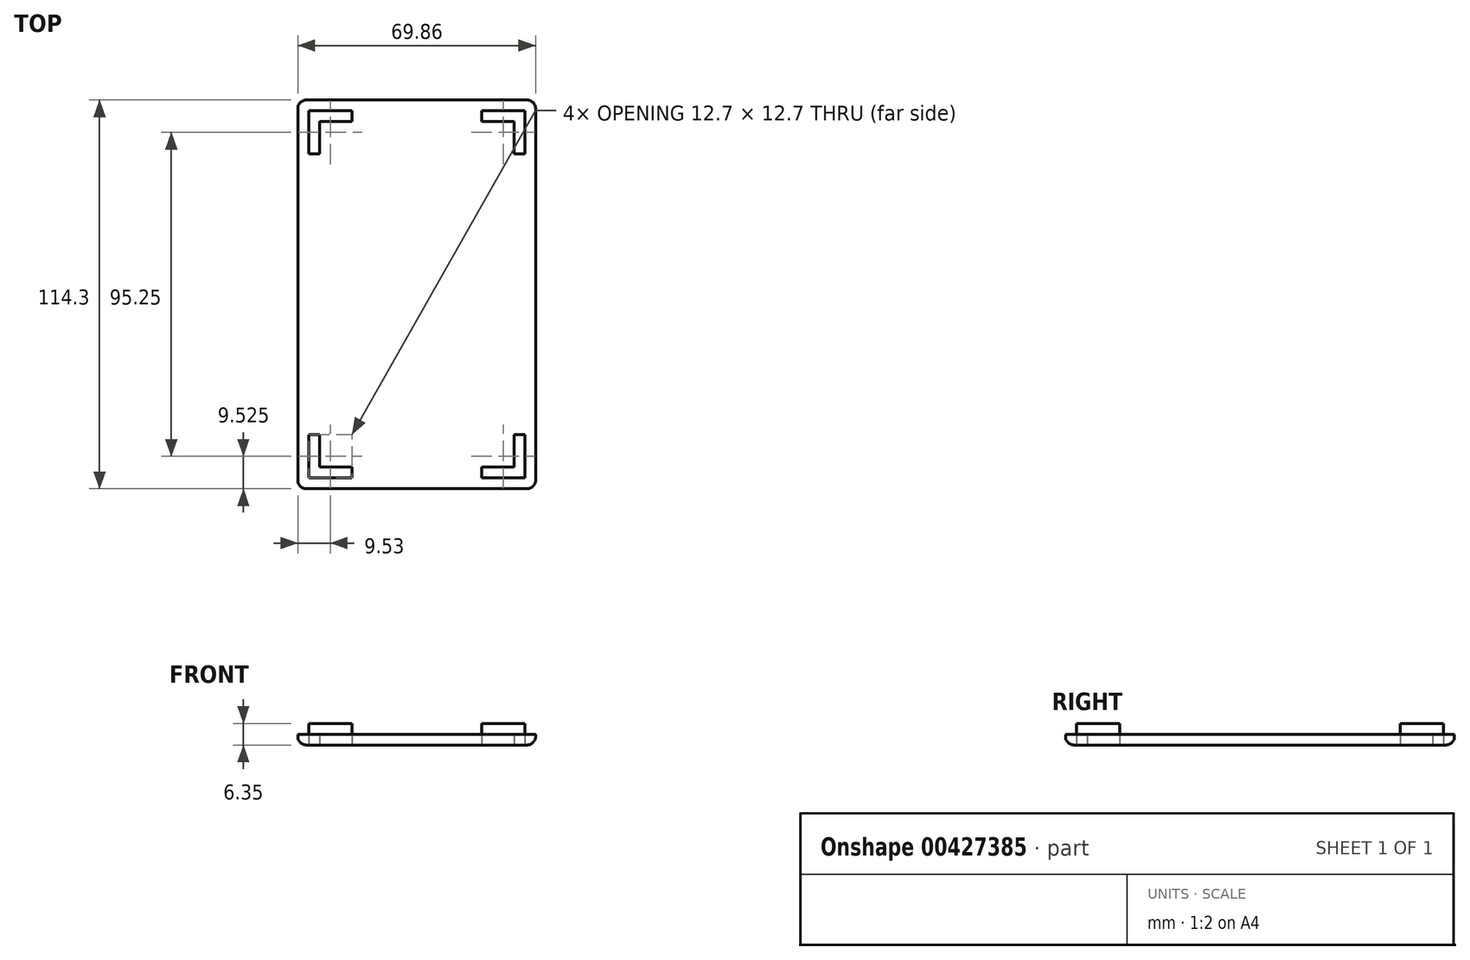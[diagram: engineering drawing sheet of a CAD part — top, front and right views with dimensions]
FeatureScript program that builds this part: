
annotation { "Feature Type Name" : "Feature", "Feature Type Description" : "" }
export const myFeature = defineFeature(function(context is Context, id is Id, definition is map)
    precondition{}
    {
        {
            var Q0;
            Q0=qCreatedBy(makeId("Top.planeOp"),FACE);
            var sketch = newSketch(context, id + "F0", { "sketchPlane" : qUnion([Q0])});
            skLineSegment(sketch, "E0.bottom", {"start": v(-34.92, 57.15) * mm, "end": v(34.93, 57.15) * mm});
            skLineSegment(sketch, "E0.top", {"start": v(-34.93, -57.15) * mm, "end": v(34.92, -57.15) * mm});
            skLineSegment(sketch, "E0.left", {"start": v(-34.92, 57.15) * mm, "end": v(-34.93, -57.15) * mm});
            skLineSegment(sketch, "E0.right", {"start": v(34.93, 57.15) * mm, "end": v(34.92, -57.15) * mm});
            skPoint(sketch, "E0.middle", {"position": v(0, 0) * mm});
            skLineSegment(sketch, "E1.bottom", {"start": v(-31.75, 53.98) * mm, "end": v(-19.05, 53.98) * mm});
            skLineSegment(sketch, "E1.top", {"start": v(-31.75, -53.98) * mm, "end": v(-19.05, -53.98) * mm});
            skLineSegment(sketch, "E1.right", {"start": v(31.75, 53.98) * mm, "end": v(31.75, 41.28) * mm});
            skLineSegment(sketch, "E2.bottom", {"start": v(-28.58, 50.8) * mm, "end": v(-19.05, 50.8) * mm});
            skLineSegment(sketch, "E2.top", {"start": v(-28.58, -50.8) * mm, "end": v(-19.05, -50.8) * mm});
            skLineSegment(sketch, "E2.left", {"start": v(-28.57, 50.8) * mm, "end": v(-28.57, 41.28) * mm});
            skLineSegment(sketch, "E2.right", {"start": v(28.58, 50.8) * mm, "end": v(28.58, 41.28) * mm});
            skLineSegment(sketch, "E3", {"start": v(-28.58, 41.28) * mm, "end": v(-31.75, 41.28) * mm});
            skLineSegment(sketch, "E4", {"start": v(-19.05, 53.98) * mm, "end": v(-19.05, 50.8) * mm});
            skLineSegment(sketch, "E5", {"start": v(19.05, 53.98) * mm, "end": v(19.05, 50.8) * mm});
            skLineSegment(sketch, "E6", {"start": v(28.58, 41.28) * mm, "end": v(31.75, 41.28) * mm});
            skLineSegment(sketch, "E7", {"start": v(28.58, -41.28) * mm, "end": v(31.75, -41.28) * mm});
            skLineSegment(sketch, "E8", {"start": v(19.05, -50.8) * mm, "end": v(19.05, -53.98) * mm});
            skLineSegment(sketch, "E9", {"start": v(-19.05, -50.8) * mm, "end": v(-19.05, -53.98) * mm});
            skLineSegment(sketch, "E10", {"start": v(-31.75, -41.28) * mm, "end": v(-28.58, -41.28) * mm});
            skLineSegment(sketch, "E11.trimOffspring", {"start": v(19.05, 53.98) * mm, "end": v(31.75, 53.98) * mm});
            skLineSegment(sketch, "E12.trimOffspring", {"start": v(19.05, 50.8) * mm, "end": v(28.58, 50.8) * mm});
            skLineSegment(sketch, "E13.trimOffspring", {"start": v(-31.75, -41.28) * mm, "end": v(-31.75, -53.98) * mm});
            skLineSegment(sketch, "E14.trimOffspring", {"start": v(-28.58, -41.28) * mm, "end": v(-28.58, -50.8) * mm});
            skLineSegment(sketch, "E15.trimOffspring", {"start": v(19.05, -50.8) * mm, "end": v(28.58, -50.8) * mm});
            skLineSegment(sketch, "E16.trimOffspring", {"start": v(19.05, -53.98) * mm, "end": v(31.75, -53.98) * mm});
            skLineSegment(sketch, "E17.trimOffspring", {"start": v(28.57, -41.28) * mm, "end": v(28.57, -50.8) * mm});
            skLineSegment(sketch, "E18.trimOffspring", {"start": v(31.75, -41.28) * mm, "end": v(31.75, -53.98) * mm});
            skLineSegment(sketch, "E19", {"start": v(-31.75, 41.28) * mm, "end": v(-31.75, 53.98) * mm});
            skSolve(sketch);
        }
        {
            var Q0;
            Q0=makeQuery(id+"F0.imprint","IMPRINT",FACE,{"disambiguationData":[TD([[makeQuery(id+"F0.imprint","IMPRINT",EDGE,{"derivedFrom":sQuery(id+"F0.wireOp",EDGE,"E1.bottom")}),-1.0]])]});
            var Q1;
            Q1=makeQuery(id+"F0.imprint","IMPRINT",FACE,{"disambiguationData":[TD([[makeQuery(id+"F0.imprint","IMPRINT",EDGE,{"derivedFrom":sQuery(id+"F0.wireOp",EDGE,"E1.right")}),-1.0]])]});
            var Q2;
            Q2=makeQuery(id+"F0.imprint","IMPRINT",FACE,{"disambiguationData":[TD([[makeQuery(id+"F0.imprint","IMPRINT",EDGE,{"derivedFrom":sQuery(id+"F0.wireOp",EDGE,"E7")}),-1.0]])]});
            var Q3;
            Q3=makeQuery(id+"F0.imprint","IMPRINT",FACE,{"disambiguationData":[TD([[makeQuery(id+"F0.imprint","IMPRINT",EDGE,{"derivedFrom":sQuery(id+"F0.wireOp",EDGE,"E1.top")}),1.0]])]});
            extrude(context, id + "F1", {"entities" : qUnion([Q0, Q1, Q2, Q3]), "depth" : 6.35 * mm});
        }
        {
            var Q0;
            Q0=makeQuery(id+"F0.imprint","IMPRINT",FACE,{"disambiguationData":[TD([[makeQuery(id+"F0.imprint","IMPRINT",EDGE,{"derivedFrom":sQuery(id+"F0.wireOp",EDGE,"E0.bottom")}),-1.0]])]});
            extrude(context, id + "F2", {"entities" : qUnion([Q0]), "depth" : 3.17 * mm});
        }
        {
            var Q0;
            Q0=makeQuery(id+"F2.opExtrude","SWEPT_EDGE",EDGE,{"disambiguationData":[OSD([sQuery(id+"F0.wireOp",EDGE,"E0.top"),sQuery(id+"F0.wireOp",EDGE,"E0.left")])]});
            var Q1;
            Q1=makeQuery(id+"F2.opExtrude","SWEPT_EDGE",EDGE,{"disambiguationData":[OSD([sQuery(id+"F0.wireOp",EDGE,"E0.bottom"),sQuery(id+"F0.wireOp",EDGE,"E0.left")])]});
            var Q2;
            Q2=makeQuery(id+"F2.opExtrude","SWEPT_EDGE",EDGE,{"disambiguationData":[OSD([sQuery(id+"F0.wireOp",EDGE,"E0.bottom"),sQuery(id+"F0.wireOp",EDGE,"E0.right")])]});
            var Q3;
            Q3=makeQuery(id+"F2.opExtrude","SWEPT_EDGE",EDGE,{"disambiguationData":[OSD([sQuery(id+"F0.wireOp",EDGE,"E0.top"),sQuery(id+"F0.wireOp",EDGE,"E0.right")])]});
            fillet(context, id + "F3", {"entities" : qUnion([Q0, Q1, Q2, Q3]), "radius" : 2.5 * mm, "tangentPropagation" : true, "allowEdgeOverflow" : false});
        }
        {
            var Q0;
            Q0=makeQuery(id+"F2.opExtrude","CAP_EDGE",EDGE,{"disambiguationData":[OSD([sQuery(id+"F0.wireOp",EDGE,"E0.top")])],"isStart":true});
            var Q1;
            {var subQ0=sQuery(id+"F0.wireOp",EDGE,"E0.right");var subQ1=sQuery(id+"F0.wireOp",EDGE,"E0.top");Q1=makeQuery(id+"F3.opFillet","BLEND_EDGE",EDGE,{"blendedFrom":[makeQuery(id+"F2.opExtrude","SWEPT_EDGE",EDGE,{"disambiguationData":[OSD([subQ1,subQ0])]}),makeQuery(id+"F2.opExtrude","CAP_FACE",FACE,{"disambiguationData":[OSD([sQuery(id+"F0.wireOp",EDGE,"E0.bottom"),subQ1,sQuery(id+"F0.wireOp",EDGE,"E0.left"),subQ0,sQuery(id+"F0.wireOp",EDGE,"E1.bottom"),sQuery(id+"F0.wireOp",EDGE,"E1.top"),sQuery(id+"F0.wireOp",EDGE,"E1.right"),sQuery(id+"F0.wireOp",EDGE,"E2.bottom"),sQuery(id+"F0.wireOp",EDGE,"E2.top"),sQuery(id+"F0.wireOp",EDGE,"E2.left"),sQuery(id+"F0.wireOp",EDGE,"E2.right"),sQuery(id+"F0.wireOp",EDGE,"E3"),sQuery(id+"F0.wireOp",EDGE,"E4"),sQuery(id+"F0.wireOp",EDGE,"E5"),sQuery(id+"F0.wireOp",EDGE,"E6"),sQuery(id+"F0.wireOp",EDGE,"E7"),sQuery(id+"F0.wireOp",EDGE,"E8"),sQuery(id+"F0.wireOp",EDGE,"E9"),sQuery(id+"F0.wireOp",EDGE,"E10"),sQuery(id+"F0.wireOp",EDGE,"E11.trimOffspring"),sQuery(id+"F0.wireOp",EDGE,"E12.trimOffspring"),sQuery(id+"F0.wireOp",EDGE,"E13.trimOffspring"),sQuery(id+"F0.wireOp",EDGE,"E14.trimOffspring"),sQuery(id+"F0.wireOp",EDGE,"E15.trimOffspring"),sQuery(id+"F0.wireOp",EDGE,"E16.trimOffspring"),sQuery(id+"F0.wireOp",EDGE,"E17.trimOffspring"),sQuery(id+"F0.wireOp",EDGE,"E18.trimOffspring"),sQuery(id+"F0.wireOp",EDGE,"E19")])],"isStart":true})],"blendedInto":[makeQuery(id+"F2.opExtrude","CAP_FACE",FACE,{"disambiguationData":[OSD([sQuery(id+"F0.wireOp",EDGE,"E0.bottom"),subQ1,sQuery(id+"F0.wireOp",EDGE,"E0.left"),subQ0,sQuery(id+"F0.wireOp",EDGE,"E1.bottom"),sQuery(id+"F0.wireOp",EDGE,"E1.top"),sQuery(id+"F0.wireOp",EDGE,"E1.right"),sQuery(id+"F0.wireOp",EDGE,"E2.bottom"),sQuery(id+"F0.wireOp",EDGE,"E2.top"),sQuery(id+"F0.wireOp",EDGE,"E2.left"),sQuery(id+"F0.wireOp",EDGE,"E2.right"),sQuery(id+"F0.wireOp",EDGE,"E3"),sQuery(id+"F0.wireOp",EDGE,"E4"),sQuery(id+"F0.wireOp",EDGE,"E5"),sQuery(id+"F0.wireOp",EDGE,"E6"),sQuery(id+"F0.wireOp",EDGE,"E7"),sQuery(id+"F0.wireOp",EDGE,"E8"),sQuery(id+"F0.wireOp",EDGE,"E9"),sQuery(id+"F0.wireOp",EDGE,"E10"),sQuery(id+"F0.wireOp",EDGE,"E11.trimOffspring"),sQuery(id+"F0.wireOp",EDGE,"E12.trimOffspring"),sQuery(id+"F0.wireOp",EDGE,"E13.trimOffspring"),sQuery(id+"F0.wireOp",EDGE,"E14.trimOffspring"),sQuery(id+"F0.wireOp",EDGE,"E15.trimOffspring"),sQuery(id+"F0.wireOp",EDGE,"E16.trimOffspring"),sQuery(id+"F0.wireOp",EDGE,"E17.trimOffspring"),sQuery(id+"F0.wireOp",EDGE,"E18.trimOffspring"),sQuery(id+"F0.wireOp",EDGE,"E19")])],"isStart":true})]});}
            var Q2;
            Q2=makeQuery(id+"F2.opExtrude","CAP_EDGE",EDGE,{"disambiguationData":[OSD([sQuery(id+"F0.wireOp",EDGE,"E0.right")])],"isStart":true});
            var Q3;
            {var subQ0=sQuery(id+"F0.wireOp",EDGE,"E0.right");var subQ1=sQuery(id+"F0.wireOp",EDGE,"E0.bottom");Q3=makeQuery(id+"F3.opFillet","BLEND_EDGE",EDGE,{"blendedFrom":[makeQuery(id+"F2.opExtrude","SWEPT_EDGE",EDGE,{"disambiguationData":[OSD([subQ1,subQ0])]}),makeQuery(id+"F2.opExtrude","CAP_FACE",FACE,{"disambiguationData":[OSD([subQ1,sQuery(id+"F0.wireOp",EDGE,"E0.top"),sQuery(id+"F0.wireOp",EDGE,"E0.left"),subQ0,sQuery(id+"F0.wireOp",EDGE,"E1.bottom"),sQuery(id+"F0.wireOp",EDGE,"E1.top"),sQuery(id+"F0.wireOp",EDGE,"E1.right"),sQuery(id+"F0.wireOp",EDGE,"E2.bottom"),sQuery(id+"F0.wireOp",EDGE,"E2.top"),sQuery(id+"F0.wireOp",EDGE,"E2.left"),sQuery(id+"F0.wireOp",EDGE,"E2.right"),sQuery(id+"F0.wireOp",EDGE,"E3"),sQuery(id+"F0.wireOp",EDGE,"E4"),sQuery(id+"F0.wireOp",EDGE,"E5"),sQuery(id+"F0.wireOp",EDGE,"E6"),sQuery(id+"F0.wireOp",EDGE,"E7"),sQuery(id+"F0.wireOp",EDGE,"E8"),sQuery(id+"F0.wireOp",EDGE,"E9"),sQuery(id+"F0.wireOp",EDGE,"E10"),sQuery(id+"F0.wireOp",EDGE,"E11.trimOffspring"),sQuery(id+"F0.wireOp",EDGE,"E12.trimOffspring"),sQuery(id+"F0.wireOp",EDGE,"E13.trimOffspring"),sQuery(id+"F0.wireOp",EDGE,"E14.trimOffspring"),sQuery(id+"F0.wireOp",EDGE,"E15.trimOffspring"),sQuery(id+"F0.wireOp",EDGE,"E16.trimOffspring"),sQuery(id+"F0.wireOp",EDGE,"E17.trimOffspring"),sQuery(id+"F0.wireOp",EDGE,"E18.trimOffspring"),sQuery(id+"F0.wireOp",EDGE,"E19")])],"isStart":true})],"blendedInto":[makeQuery(id+"F2.opExtrude","CAP_FACE",FACE,{"disambiguationData":[OSD([subQ1,sQuery(id+"F0.wireOp",EDGE,"E0.top"),sQuery(id+"F0.wireOp",EDGE,"E0.left"),subQ0,sQuery(id+"F0.wireOp",EDGE,"E1.bottom"),sQuery(id+"F0.wireOp",EDGE,"E1.top"),sQuery(id+"F0.wireOp",EDGE,"E1.right"),sQuery(id+"F0.wireOp",EDGE,"E2.bottom"),sQuery(id+"F0.wireOp",EDGE,"E2.top"),sQuery(id+"F0.wireOp",EDGE,"E2.left"),sQuery(id+"F0.wireOp",EDGE,"E2.right"),sQuery(id+"F0.wireOp",EDGE,"E3"),sQuery(id+"F0.wireOp",EDGE,"E4"),sQuery(id+"F0.wireOp",EDGE,"E5"),sQuery(id+"F0.wireOp",EDGE,"E6"),sQuery(id+"F0.wireOp",EDGE,"E7"),sQuery(id+"F0.wireOp",EDGE,"E8"),sQuery(id+"F0.wireOp",EDGE,"E9"),sQuery(id+"F0.wireOp",EDGE,"E10"),sQuery(id+"F0.wireOp",EDGE,"E11.trimOffspring"),sQuery(id+"F0.wireOp",EDGE,"E12.trimOffspring"),sQuery(id+"F0.wireOp",EDGE,"E13.trimOffspring"),sQuery(id+"F0.wireOp",EDGE,"E14.trimOffspring"),sQuery(id+"F0.wireOp",EDGE,"E15.trimOffspring"),sQuery(id+"F0.wireOp",EDGE,"E16.trimOffspring"),sQuery(id+"F0.wireOp",EDGE,"E17.trimOffspring"),sQuery(id+"F0.wireOp",EDGE,"E18.trimOffspring"),sQuery(id+"F0.wireOp",EDGE,"E19")])],"isStart":true})]});}
            var Q4;
            Q4=makeQuery(id+"F2.opExtrude","CAP_EDGE",EDGE,{"disambiguationData":[OSD([sQuery(id+"F0.wireOp",EDGE,"E0.left")])],"isStart":true});
            var Q5;
            {var subQ0=sQuery(id+"F0.wireOp",EDGE,"E0.left");var subQ1=sQuery(id+"F0.wireOp",EDGE,"E0.top");Q5=makeQuery(id+"F3.opFillet","BLEND_EDGE",EDGE,{"blendedFrom":[makeQuery(id+"F2.opExtrude","SWEPT_EDGE",EDGE,{"disambiguationData":[OSD([subQ1,subQ0])]}),makeQuery(id+"F2.opExtrude","CAP_FACE",FACE,{"disambiguationData":[OSD([sQuery(id+"F0.wireOp",EDGE,"E0.bottom"),subQ1,subQ0,sQuery(id+"F0.wireOp",EDGE,"E0.right"),sQuery(id+"F0.wireOp",EDGE,"E1.bottom"),sQuery(id+"F0.wireOp",EDGE,"E1.top"),sQuery(id+"F0.wireOp",EDGE,"E1.right"),sQuery(id+"F0.wireOp",EDGE,"E2.bottom"),sQuery(id+"F0.wireOp",EDGE,"E2.top"),sQuery(id+"F0.wireOp",EDGE,"E2.left"),sQuery(id+"F0.wireOp",EDGE,"E2.right"),sQuery(id+"F0.wireOp",EDGE,"E3"),sQuery(id+"F0.wireOp",EDGE,"E4"),sQuery(id+"F0.wireOp",EDGE,"E5"),sQuery(id+"F0.wireOp",EDGE,"E6"),sQuery(id+"F0.wireOp",EDGE,"E7"),sQuery(id+"F0.wireOp",EDGE,"E8"),sQuery(id+"F0.wireOp",EDGE,"E9"),sQuery(id+"F0.wireOp",EDGE,"E10"),sQuery(id+"F0.wireOp",EDGE,"E11.trimOffspring"),sQuery(id+"F0.wireOp",EDGE,"E12.trimOffspring"),sQuery(id+"F0.wireOp",EDGE,"E13.trimOffspring"),sQuery(id+"F0.wireOp",EDGE,"E14.trimOffspring"),sQuery(id+"F0.wireOp",EDGE,"E15.trimOffspring"),sQuery(id+"F0.wireOp",EDGE,"E16.trimOffspring"),sQuery(id+"F0.wireOp",EDGE,"E17.trimOffspring"),sQuery(id+"F0.wireOp",EDGE,"E18.trimOffspring"),sQuery(id+"F0.wireOp",EDGE,"E19")])],"isStart":true})],"blendedInto":[makeQuery(id+"F2.opExtrude","CAP_FACE",FACE,{"disambiguationData":[OSD([sQuery(id+"F0.wireOp",EDGE,"E0.bottom"),subQ1,subQ0,sQuery(id+"F0.wireOp",EDGE,"E0.right"),sQuery(id+"F0.wireOp",EDGE,"E1.bottom"),sQuery(id+"F0.wireOp",EDGE,"E1.top"),sQuery(id+"F0.wireOp",EDGE,"E1.right"),sQuery(id+"F0.wireOp",EDGE,"E2.bottom"),sQuery(id+"F0.wireOp",EDGE,"E2.top"),sQuery(id+"F0.wireOp",EDGE,"E2.left"),sQuery(id+"F0.wireOp",EDGE,"E2.right"),sQuery(id+"F0.wireOp",EDGE,"E3"),sQuery(id+"F0.wireOp",EDGE,"E4"),sQuery(id+"F0.wireOp",EDGE,"E5"),sQuery(id+"F0.wireOp",EDGE,"E6"),sQuery(id+"F0.wireOp",EDGE,"E7"),sQuery(id+"F0.wireOp",EDGE,"E8"),sQuery(id+"F0.wireOp",EDGE,"E9"),sQuery(id+"F0.wireOp",EDGE,"E10"),sQuery(id+"F0.wireOp",EDGE,"E11.trimOffspring"),sQuery(id+"F0.wireOp",EDGE,"E12.trimOffspring"),sQuery(id+"F0.wireOp",EDGE,"E13.trimOffspring"),sQuery(id+"F0.wireOp",EDGE,"E14.trimOffspring"),sQuery(id+"F0.wireOp",EDGE,"E15.trimOffspring"),sQuery(id+"F0.wireOp",EDGE,"E16.trimOffspring"),sQuery(id+"F0.wireOp",EDGE,"E17.trimOffspring"),sQuery(id+"F0.wireOp",EDGE,"E18.trimOffspring"),sQuery(id+"F0.wireOp",EDGE,"E19")])],"isStart":true})]});}
            var Q6;
            Q6=makeQuery(id+"F2.opExtrude","CAP_EDGE",EDGE,{"disambiguationData":[OSD([sQuery(id+"F0.wireOp",EDGE,"E0.bottom")])],"isStart":true});
            var Q7;
            {var subQ0=sQuery(id+"F0.wireOp",EDGE,"E0.left");var subQ1=sQuery(id+"F0.wireOp",EDGE,"E0.bottom");Q7=makeQuery(id+"F3.opFillet","BLEND_EDGE",EDGE,{"blendedFrom":[makeQuery(id+"F2.opExtrude","SWEPT_EDGE",EDGE,{"disambiguationData":[OSD([subQ1,subQ0])]}),makeQuery(id+"F2.opExtrude","CAP_FACE",FACE,{"disambiguationData":[OSD([subQ1,sQuery(id+"F0.wireOp",EDGE,"E0.top"),subQ0,sQuery(id+"F0.wireOp",EDGE,"E0.right"),sQuery(id+"F0.wireOp",EDGE,"E1.bottom"),sQuery(id+"F0.wireOp",EDGE,"E1.top"),sQuery(id+"F0.wireOp",EDGE,"E1.right"),sQuery(id+"F0.wireOp",EDGE,"E2.bottom"),sQuery(id+"F0.wireOp",EDGE,"E2.top"),sQuery(id+"F0.wireOp",EDGE,"E2.left"),sQuery(id+"F0.wireOp",EDGE,"E2.right"),sQuery(id+"F0.wireOp",EDGE,"E3"),sQuery(id+"F0.wireOp",EDGE,"E4"),sQuery(id+"F0.wireOp",EDGE,"E5"),sQuery(id+"F0.wireOp",EDGE,"E6"),sQuery(id+"F0.wireOp",EDGE,"E7"),sQuery(id+"F0.wireOp",EDGE,"E8"),sQuery(id+"F0.wireOp",EDGE,"E9"),sQuery(id+"F0.wireOp",EDGE,"E10"),sQuery(id+"F0.wireOp",EDGE,"E11.trimOffspring"),sQuery(id+"F0.wireOp",EDGE,"E12.trimOffspring"),sQuery(id+"F0.wireOp",EDGE,"E13.trimOffspring"),sQuery(id+"F0.wireOp",EDGE,"E14.trimOffspring"),sQuery(id+"F0.wireOp",EDGE,"E15.trimOffspring"),sQuery(id+"F0.wireOp",EDGE,"E16.trimOffspring"),sQuery(id+"F0.wireOp",EDGE,"E17.trimOffspring"),sQuery(id+"F0.wireOp",EDGE,"E18.trimOffspring"),sQuery(id+"F0.wireOp",EDGE,"E19")])],"isStart":true})],"blendedInto":[makeQuery(id+"F2.opExtrude","CAP_FACE",FACE,{"disambiguationData":[OSD([subQ1,sQuery(id+"F0.wireOp",EDGE,"E0.top"),subQ0,sQuery(id+"F0.wireOp",EDGE,"E0.right"),sQuery(id+"F0.wireOp",EDGE,"E1.bottom"),sQuery(id+"F0.wireOp",EDGE,"E1.top"),sQuery(id+"F0.wireOp",EDGE,"E1.right"),sQuery(id+"F0.wireOp",EDGE,"E2.bottom"),sQuery(id+"F0.wireOp",EDGE,"E2.top"),sQuery(id+"F0.wireOp",EDGE,"E2.left"),sQuery(id+"F0.wireOp",EDGE,"E2.right"),sQuery(id+"F0.wireOp",EDGE,"E3"),sQuery(id+"F0.wireOp",EDGE,"E4"),sQuery(id+"F0.wireOp",EDGE,"E5"),sQuery(id+"F0.wireOp",EDGE,"E6"),sQuery(id+"F0.wireOp",EDGE,"E7"),sQuery(id+"F0.wireOp",EDGE,"E8"),sQuery(id+"F0.wireOp",EDGE,"E9"),sQuery(id+"F0.wireOp",EDGE,"E10"),sQuery(id+"F0.wireOp",EDGE,"E11.trimOffspring"),sQuery(id+"F0.wireOp",EDGE,"E12.trimOffspring"),sQuery(id+"F0.wireOp",EDGE,"E13.trimOffspring"),sQuery(id+"F0.wireOp",EDGE,"E14.trimOffspring"),sQuery(id+"F0.wireOp",EDGE,"E15.trimOffspring"),sQuery(id+"F0.wireOp",EDGE,"E16.trimOffspring"),sQuery(id+"F0.wireOp",EDGE,"E17.trimOffspring"),sQuery(id+"F0.wireOp",EDGE,"E18.trimOffspring"),sQuery(id+"F0.wireOp",EDGE,"E19")])],"isStart":true})]});}
            fillet(context, id + "F4", {"entities" : qUnion([Q0, Q1, Q2, Q3, Q4, Q5, Q6, Q7]), "radius" : 2.5 * mm, "tangentPropagation" : true, "allowEdgeOverflow" : false});
        }
    });
